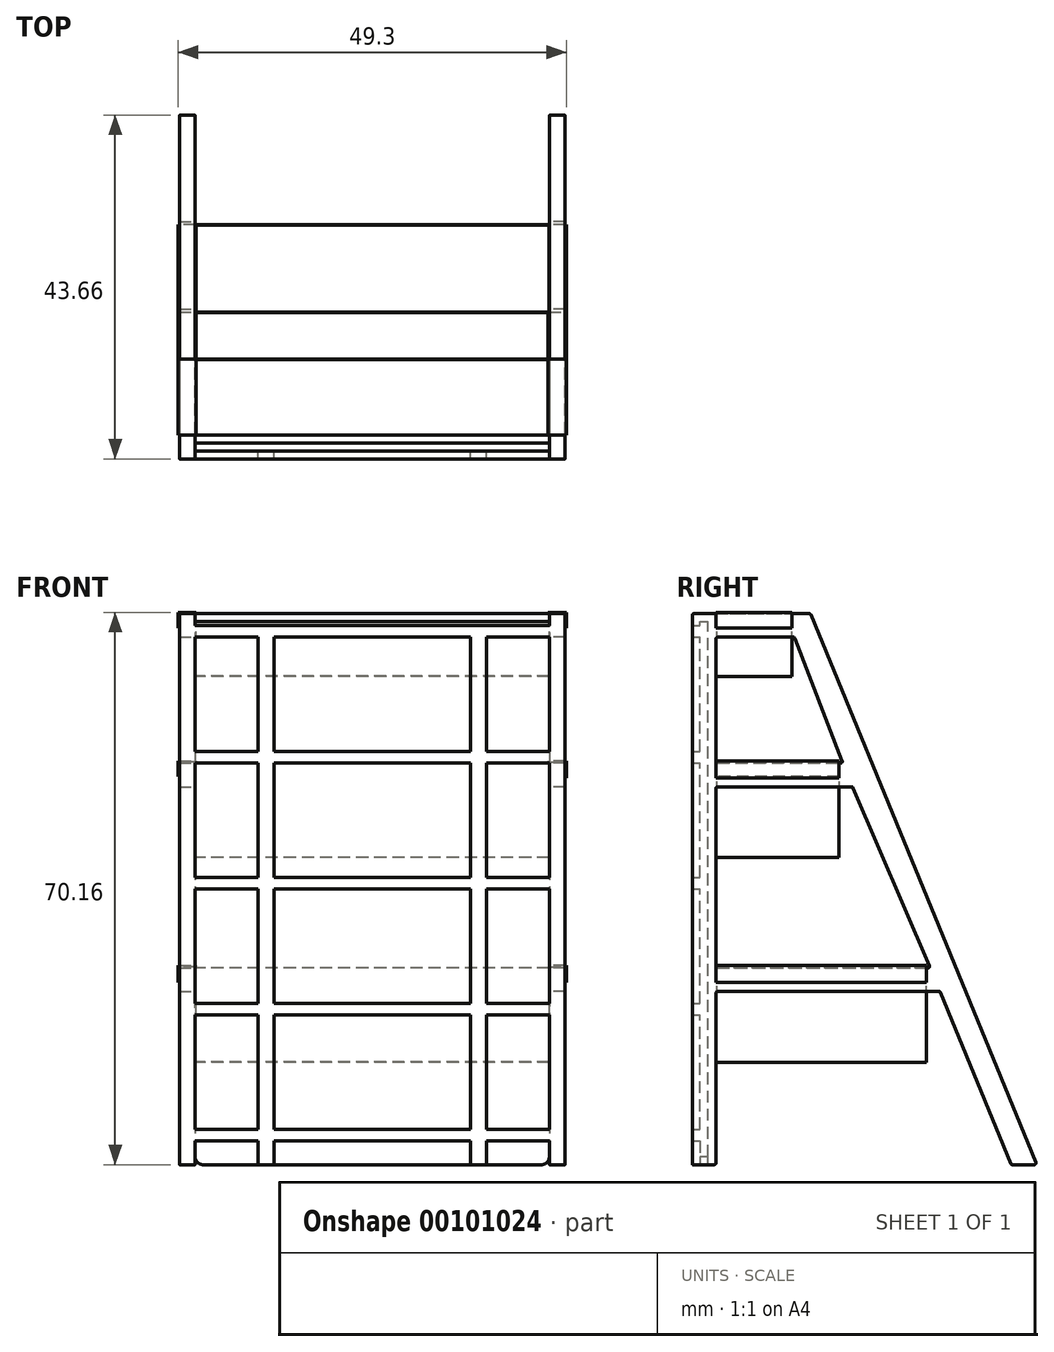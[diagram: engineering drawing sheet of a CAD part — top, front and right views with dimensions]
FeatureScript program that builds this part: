
annotation { "Feature Type Name" : "Feature", "Feature Type Description" : "" }
export const myFeature = defineFeature(function(context is Context, id is Id, definition is map)
    precondition{}
    {
        {
            var Q0;
            Q0=qCreatedBy(makeId("Right.planeOp"),FACE);
            var sketch = newSketch(context, id + "F0", { "sketchPlane" : qUnion([Q0])});
            skLineSegment(sketch, "E0", {"start": v(0, 0.2) * mm, "end": v(0, 69.8) * mm});
            skLineSegment(sketch, "E1", {"start": v(0.2, 70) * mm, "end": v(14.87, 70) * mm});
            skLineSegment(sketch, "E2", {"start": v(15.05, 69.88) * mm, "end": v(43.64, 0.28) * mm});
            skLineSegment(sketch, "E3", {"start": v(43.46, 0) * mm, "end": v(40.65, 0) * mm});
            skLineSegment(sketch, "E4", {"start": v(12.86, 67) * mm, "end": v(3.2, 67) * mm});
            skLineSegment(sketch, "E5", {"start": v(2.8, 0) * mm, "end": v(0.2, 0) * mm});
            skLineSegment(sketch, "E6", {"start": v(3.2, 51) * mm, "end": v(18.85, 51) * mm});
            skLineSegment(sketch, "E7", {"start": v(13.04, 66.87) * mm, "end": v(19.04, 51.27) * mm});
            skLineSegment(sketch, "E8", {"start": v(3, 66.8) * mm, "end": v(3, 51.2) * mm});
            skLineSegment(sketch, "E9", {"start": v(3.2, 48) * mm, "end": v(20.25, 48) * mm});
            skLineSegment(sketch, "E10", {"start": v(3, 47.8) * mm, "end": v(3, 25.2) * mm});
            skLineSegment(sketch, "E11", {"start": v(3.2, 25) * mm, "end": v(29.94, 25) * mm});
            skLineSegment(sketch, "E12", {"start": v(3.2, 22) * mm, "end": v(31.34, 22) * mm});
            skLineSegment(sketch, "E13", {"start": v(70.75, 0) * mm, "end": v(70.75, 13) * mm});
            skLineSegment(sketch, "E14", {"start": v(70.75, 13) * mm, "end": v(70.75, 25) * mm});
            skLineSegment(sketch, "E15", {"start": v(70.75, 25) * mm, "end": v(70.75, 40) * mm});
            skLineSegment(sketch, "E16", {"start": v(70.75, 40) * mm, "end": v(70.75, 52) * mm});
            skLineSegment(sketch, "E17", {"start": v(70.75, 52) * mm, "end": v(70.75, 62) * mm});
            skLineSegment(sketch, "E18", {"start": v(70.75, 62) * mm, "end": v(70.75, 70) * mm});
            skLineSegment(sketch, "E19", {"start": v(3, 0.2) * mm, "end": v(3, 21.8) * mm});
            skLineSegment(sketch, "E20", {"start": v(20.43, 47.88) * mm, "end": v(30.13, 25.28) * mm});
            skLineSegment(sketch, "E21", {"start": v(31.53, 21.88) * mm, "end": v(40.46, 0.12) * mm});
            skPoint(sketch, "E22.visualSharp", {"position": v(3, 25) * mm});
            skArc(sketch, "E22.filletArc", {"start": v(3, 25.2) * mm, "mid": v(3.06, 25.06) * mm, "end": v(3.2, 25) * mm});
            skPoint(sketch, "E23.visualSharp", {"position": v(3, 22) * mm});
            skArc(sketch, "E23.filletArc", {"start": v(3.2, 22) * mm, "mid": v(3.06, 21.94) * mm, "end": v(3, 21.8) * mm});
            skPoint(sketch, "E24.visualSharp", {"position": v(31.48, 22) * mm});
            skArc(sketch, "E24.filletArc", {"start": v(31.53, 21.88) * mm, "mid": v(31.45, 21.97) * mm, "end": v(31.34, 22) * mm});
            skPoint(sketch, "E25.visualSharp", {"position": v(3, 0) * mm});
            skArc(sketch, "E25.filletArc", {"start": v(2.8, 0) * mm, "mid": v(2.94, 0.06) * mm, "end": v(3, 0.2) * mm});
            skPoint(sketch, "E26.visualSharp", {"position": v(40.51, 0) * mm});
            skArc(sketch, "E26.filletArc", {"start": v(40.46, 0.12) * mm, "mid": v(40.54, 0.03) * mm, "end": v(40.65, 0) * mm});
            skPoint(sketch, "E27.visualSharp", {"position": v(15, 70) * mm});
            skArc(sketch, "E27.filletArc", {"start": v(15.05, 69.88) * mm, "mid": v(14.98, 69.97) * mm, "end": v(14.87, 70) * mm});
            skPoint(sketch, "E28.visualSharp", {"position": v(0, 70) * mm});
            skArc(sketch, "E28.filletArc", {"start": v(0.2, 70) * mm, "mid": v(0.06, 69.94) * mm, "end": v(0, 69.8) * mm});
            skPoint(sketch, "E29.visualSharp", {"position": v(3, 67) * mm});
            skArc(sketch, "E29.filletArc", {"start": v(3.2, 67) * mm, "mid": v(3.06, 66.94) * mm, "end": v(3, 66.8) * mm});
            skPoint(sketch, "E30.visualSharp", {"position": v(19.14, 51) * mm});
            skArc(sketch, "E30.filletArc", {"start": v(18.85, 51) * mm, "mid": v(19.02, 51.09) * mm, "end": v(19.04, 51.27) * mm});
            skPoint(sketch, "E31.visualSharp", {"position": v(3, 51) * mm});
            skArc(sketch, "E31.filletArc", {"start": v(3, 51.2) * mm, "mid": v(3.06, 51.06) * mm, "end": v(3.2, 51) * mm});
            skPoint(sketch, "E32.visualSharp", {"position": v(20.38, 48) * mm});
            skArc(sketch, "E32.filletArc", {"start": v(20.43, 47.88) * mm, "mid": v(20.36, 47.97) * mm, "end": v(20.25, 48) * mm});
            skPoint(sketch, "E33.visualSharp", {"position": v(3, 48) * mm});
            skArc(sketch, "E33.filletArc", {"start": v(3.2, 48) * mm, "mid": v(3.06, 47.94) * mm, "end": v(3, 47.8) * mm});
            skPoint(sketch, "E34.visualSharp", {"position": v(30.25, 25) * mm});
            skArc(sketch, "E34.filletArc", {"start": v(29.94, 25) * mm, "mid": v(30.11, 25.09) * mm, "end": v(30.13, 25.28) * mm});
            skPoint(sketch, "E35.visualSharp", {"position": v(43.76, 0) * mm});
            skArc(sketch, "E35.filletArc", {"start": v(43.46, 0) * mm, "mid": v(43.62, 0.09) * mm, "end": v(43.64, 0.28) * mm});
            skPoint(sketch, "E36.visualSharp", {"position": v(0, 0) * mm});
            skArc(sketch, "E36.filletArc", {"start": v(0, 0.2) * mm, "mid": v(0.06, 0.06) * mm, "end": v(0.2, 0) * mm});
            skPoint(sketch, "E37.visualSharp", {"position": v(13, 67) * mm});
            skArc(sketch, "E37.filletArc", {"start": v(13.04, 66.87) * mm, "mid": v(12.97, 66.96) * mm, "end": v(12.86, 67) * mm});
            skLineSegment(sketch, "E38", {"start": v(4.02, 67) * mm, "end": v(4.02, 70) * mm});
            skLineSegment(sketch, "E39.bottom", {"start": v(1, 3) * mm, "end": v(2, 3) * mm});
            skLineSegment(sketch, "E39.top", {"start": v(1, 9) * mm, "end": v(2, 9) * mm});
            skLineSegment(sketch, "E39.left", {"start": v(1, 3) * mm, "end": v(1, 9) * mm});
            skLineSegment(sketch, "E39.right", {"start": v(2, 3) * mm, "end": v(2, 9) * mm});
            skLineSegment(sketch, "E40.0.1.0", {"start": v(1, 39) * mm, "end": v(2, 39) * mm});
            skLineSegment(sketch, "E40.0.1.1", {"start": v(1, 33) * mm, "end": v(1, 39) * mm});
            skLineSegment(sketch, "E40.0.1.2", {"start": v(2, 33) * mm, "end": v(2, 39) * mm});
            skLineSegment(sketch, "E40.0.1.3", {"start": v(1, 33) * mm, "end": v(2, 33) * mm});
            skLineSegment(sketch, "E40.0.2.0", {"start": v(1, 69) * mm, "end": v(2, 69) * mm});
            skLineSegment(sketch, "E40.0.2.1", {"start": v(1, 63) * mm, "end": v(1, 69) * mm});
            skLineSegment(sketch, "E40.0.2.2", {"start": v(2, 63) * mm, "end": v(2, 69) * mm});
            skLineSegment(sketch, "E40.0.2.3", {"start": v(1, 63) * mm, "end": v(2, 63) * mm});
            skLineSegment(sketch, "E40.direction1", {"start": v(1, 9) * mm, "end": v(26, 9) * mm, "construction": true});
            skLineSegment(sketch, "E40.direction2", {"start": v(1, 9) * mm, "end": v(1, 39) * mm, "construction": true});
            skLineSegment(sketch, "E41", {"start": v(1, 3) * mm, "end": v(1, 0) * mm});
            skSolve(sketch);
        }
        {
            var Q0;
            Q0=qCreatedBy(makeId("Front.planeOp"),FACE);
            var sketch = newSketch(context, id + "F1", { "sketchPlane" : qUnion([Q0])});
            skLineSegment(sketch, "E42", {"start": v(0, 0) * mm, "end": v(0, 13) * mm});
            skLineSegment(sketch, "E43.bottom", {"start": v(0, 13) * mm, "end": v(-45, 13) * mm});
            skLineSegment(sketch, "E43.top", {"start": v(0, 25) * mm, "end": v(-45, 25) * mm});
            skLineSegment(sketch, "E43.left", {"start": v(0, 13) * mm, "end": v(0, 25) * mm});
            skLineSegment(sketch, "E43.right", {"start": v(-45, 13) * mm, "end": v(-45, 25) * mm});
            skLineSegment(sketch, "E44", {"start": v(0, 25) * mm, "end": v(0, 39) * mm});
            skLineSegment(sketch, "E45.bottom", {"start": v(0, 39) * mm, "end": v(-45, 39) * mm});
            skLineSegment(sketch, "E45.top", {"start": v(0, 51) * mm, "end": v(-45, 51) * mm});
            skLineSegment(sketch, "E45.left", {"start": v(0, 39) * mm, "end": v(0, 51) * mm});
            skLineSegment(sketch, "E45.right", {"start": v(-45, 39) * mm, "end": v(-45, 51) * mm});
            skLineSegment(sketch, "E46.bottom", {"start": v(0, 62) * mm, "end": v(-45, 62) * mm});
            skLineSegment(sketch, "E46.top", {"start": v(0, 70) * mm, "end": v(-45, 70) * mm});
            skLineSegment(sketch, "E46.left", {"start": v(0, 62) * mm, "end": v(0, 70) * mm});
            skLineSegment(sketch, "E46.right", {"start": v(-45, 62) * mm, "end": v(-45, 70) * mm});
            skLineSegment(sketch, "E47", {"start": v(0, 70) * mm, "end": v(0, 70.01) * mm});
            skLineSegment(sketch, "E48", {"start": v(0, 70.01) * mm, "end": v(2, 70.01) * mm});
            skLineSegment(sketch, "E49", {"start": v(2, 70.01) * mm, "end": v(2, 68.16) * mm});
            skLineSegment(sketch, "E50", {"start": v(2, 68.16) * mm, "end": v(2.15, 68.16) * mm});
            skLineSegment(sketch, "E51", {"start": v(2.15, 68.16) * mm, "end": v(2.15, 70.16) * mm});
            skLineSegment(sketch, "E52", {"start": v(2.15, 70.16) * mm, "end": v(-0.15, 70.16) * mm});
            skLineSegment(sketch, "E53", {"start": v(-0.15, 70.16) * mm, "end": v(-0.15, 68.16) * mm});
            skLineSegment(sketch, "E54", {"start": v(0, 69.73) * mm, "end": v(0, 70) * mm});
            skLineSegment(sketch, "E55", {"start": v(-45, 70) * mm, "end": v(-45, 70.01) * mm});
            skLineSegment(sketch, "E56", {"start": v(-45, 70.01) * mm, "end": v(-47, 70.01) * mm});
            skLineSegment(sketch, "E57", {"start": v(-47, 70.01) * mm, "end": v(-47, 68.16) * mm});
            skLineSegment(sketch, "E58", {"start": v(-47, 68.16) * mm, "end": v(-47.15, 68.16) * mm});
            skLineSegment(sketch, "E59", {"start": v(-47.15, 68.16) * mm, "end": v(-47.15, 70.16) * mm});
            skLineSegment(sketch, "E60", {"start": v(-47.15, 70.16) * mm, "end": v(-44.85, 70.16) * mm});
            skLineSegment(sketch, "E61", {"start": v(-44.85, 70.16) * mm, "end": v(-44.85, 68.16) * mm});
            skLineSegment(sketch, "E62", {"start": v(-44.85, 68.16) * mm, "end": v(-45, 68.16) * mm});
            skLineSegment(sketch, "E63", {"start": v(-45, 51) * mm, "end": v(-45, 51.15) * mm});
            skLineSegment(sketch, "E64", {"start": v(-45, 51.15) * mm, "end": v(-47, 51.15) * mm});
            skLineSegment(sketch, "E65", {"start": v(-47, 51.15) * mm, "end": v(-47, 49.3) * mm});
            skLineSegment(sketch, "E66", {"start": v(-47, 49.3) * mm, "end": v(-47.15, 49.3) * mm});
            skLineSegment(sketch, "E67", {"start": v(-47.15, 49.3) * mm, "end": v(-47.15, 51.3) * mm});
            skLineSegment(sketch, "E68", {"start": v(-47.15, 51.3) * mm, "end": v(-44.85, 51.3) * mm});
            skLineSegment(sketch, "E69", {"start": v(-44.85, 51.3) * mm, "end": v(-44.85, 51) * mm});
            skLineSegment(sketch, "E70", {"start": v(0, 51) * mm, "end": v(0, 51.15) * mm});
            skLineSegment(sketch, "E71", {"start": v(0, 51.15) * mm, "end": v(2, 51.15) * mm});
            skLineSegment(sketch, "E72", {"start": v(2, 51.15) * mm, "end": v(2, 49.15) * mm});
            skLineSegment(sketch, "E73", {"start": v(2, 49.15) * mm, "end": v(2.15, 49.15) * mm});
            skLineSegment(sketch, "E74", {"start": v(2.15, 49.15) * mm, "end": v(2.15, 51.3) * mm});
            skLineSegment(sketch, "E75", {"start": v(2.15, 51.3) * mm, "end": v(-0.15, 51.3) * mm});
            skLineSegment(sketch, "E76", {"start": v(-0.15, 51.3) * mm, "end": v(-0.15, 51) * mm});
            skLineSegment(sketch, "E77", {"start": v(0, 25) * mm, "end": v(0, 25.15) * mm});
            skLineSegment(sketch, "E78", {"start": v(0, 25.15) * mm, "end": v(2, 25.15) * mm});
            skLineSegment(sketch, "E79", {"start": v(2, 25.15) * mm, "end": v(2, 23.15) * mm});
            skLineSegment(sketch, "E80", {"start": v(2, 23.15) * mm, "end": v(2.15, 23.15) * mm});
            skLineSegment(sketch, "E81", {"start": v(2.15, 23.15) * mm, "end": v(2.15, 25.3) * mm});
            skLineSegment(sketch, "E82", {"start": v(2.15, 25.3) * mm, "end": v(-0.15, 25.3) * mm});
            skLineSegment(sketch, "E83", {"start": v(-0.15, 25.3) * mm, "end": v(-0.15, 25) * mm});
            skLineSegment(sketch, "E84", {"start": v(-45, 25) * mm, "end": v(-45, 25.15) * mm});
            skLineSegment(sketch, "E85", {"start": v(-45, 25.15) * mm, "end": v(-47, 25.15) * mm});
            skLineSegment(sketch, "E86", {"start": v(-47, 25.15) * mm, "end": v(-47, 23.15) * mm});
            skLineSegment(sketch, "E87", {"start": v(-47, 23.15) * mm, "end": v(-47.15, 23.15) * mm});
            skLineSegment(sketch, "E88", {"start": v(-47.15, 23.15) * mm, "end": v(-47.15, 25.3) * mm});
            skLineSegment(sketch, "E89", {"start": v(-47.15, 25.3) * mm, "end": v(-44.85, 25.3) * mm});
            skLineSegment(sketch, "E90", {"start": v(-44.85, 25.3) * mm, "end": v(-44.85, 25) * mm});
            skSolve(sketch);
        }
        {
            var Q0;
            Q0=makeQuery(id+"F0.imprint","IMPRINT",FACE,{"disambiguationData":[TD([[makeQuery(id+"F0.imprint","IMPRINT",EDGE,{"derivedFrom":sQuery(id+"F0.wireOp",EDGE,"E0")}),-1.0]])]});
            extrude(context, id + "F2", {"entities" : qUnion([Q0]), "depth" : 2 * mm});
        }
        {
            var Q0;
            Q0=qSketchRegion(id+"F0",true);
            extrude(context, id + "F3", {"entities" : qUnion([Q0]), "oppositeDirection" : true, "depth" : 47 * mm, "hasSecondDirection" : true, "secondDirectionOppositeDirection" : true, "secondDirectionDepth" : 45 * mm});
        }
        {
            var Q0;
            Q0=makeQuery(id+"F1.imprint","IMPRINT",FACE,{"disambiguationData":[TD([[makeQuery(id+"F1.imprint","IMPRINT",EDGE,{"derivedFrom":sQuery(id+"F1.wireOp",EDGE,"E46.bottom")}),-1.0]])]});
            var Q1;
            {var subQ0=sQuery(id+"F1.wireOp",EDGE,"E47");Q1=makeQuery(id+"F1.imprint","IMPRINT",FACE,{"disambiguationData":[TD([[makeQuery(id+"F1.imprint","IMPRINT",EDGE,{"derivedFrom":subQ0}),1.0]])]});}
            var Q2;
            {var subQ5=sQuery(id+"F1.wireOp",EDGE,"E62");Q2=makeQuery(id+"F1.imprint","IMPRINT",FACE,{"disambiguationData":[TD([[makeQuery(id+"F1.imprint","IMPRINT",EDGE,{"derivedFrom":subQ5}),-1.0]])]});}
            var Q3;
            {var subQ0=sQuery(id+"F1.wireOp",EDGE,"E55");Q3=makeQuery(id+"F1.imprint","IMPRINT",FACE,{"disambiguationData":[TD([[makeQuery(id+"F1.imprint","IMPRINT",EDGE,{"derivedFrom":subQ0}),-1.0]])]});}
            extrude(context, id + "F4", {"entities" : qUnion([Q0, Q1, Q2, Q3]), "oppositeDirection" : true, "depth" : 12.65 * mm, "hasSecondDirection" : true, "secondDirectionOppositeDirection" : true, "secondDirectionDepth" : 3 * mm});
        }
        {
            var Q0;
            Q0=makeQuery(id+"F1.imprint","IMPRINT",FACE,{"disambiguationData":[TD([[makeQuery(id+"F1.imprint","IMPRINT",EDGE,{"derivedFrom":sQuery(id+"F1.wireOp",EDGE,"E45.bottom")}),-1.0]])]});
            var Q1;
            {var subQ0=sQuery(id+"F1.wireOp",EDGE,"E70");Q1=makeQuery(id+"F1.imprint","IMPRINT",FACE,{"disambiguationData":[TD([[makeQuery(id+"F1.imprint","IMPRINT",EDGE,{"derivedFrom":subQ0}),1.0]])]});}
            var Q2;
            {var subQ0=sQuery(id+"F1.wireOp",EDGE,"E63");Q2=makeQuery(id+"F1.imprint","IMPRINT",FACE,{"disambiguationData":[TD([[makeQuery(id+"F1.imprint","IMPRINT",EDGE,{"derivedFrom":subQ0}),-1.0]])]});}
            extrude(context, id + "F5", {"entities" : qUnion([Q0, Q1, Q2]), "oppositeDirection" : true, "depth" : 18.65 * mm, "hasSecondDirection" : true, "secondDirectionOppositeDirection" : true, "secondDirectionDepth" : 3 * mm});
        }
        {
            var Q0;
            Q0=makeQuery(id+"F1.imprint","IMPRINT",FACE,{"disambiguationData":[TD([[makeQuery(id+"F1.imprint","IMPRINT",EDGE,{"derivedFrom":sQuery(id+"F1.wireOp",EDGE,"E43.bottom")}),-1.0]])]});
            var Q1;
            {var subQ0=sQuery(id+"F1.wireOp",EDGE,"E84");Q1=makeQuery(id+"F1.imprint","IMPRINT",FACE,{"disambiguationData":[TD([[makeQuery(id+"F1.imprint","IMPRINT",EDGE,{"derivedFrom":subQ0}),-1.0]])]});}
            var Q2;
            {var subQ0=sQuery(id+"F1.wireOp",EDGE,"E78");Q2=makeQuery(id+"F1.imprint","IMPRINT",FACE,{"disambiguationData":[TD([[makeQuery(id+"F1.imprint","IMPRINT",EDGE,{"derivedFrom":subQ0}),1.0]])]});}
            var Q3;
            {var subQ0=sQuery(id+"F1.wireOp",EDGE,"E77");Q3=makeQuery(id+"F1.imprint","IMPRINT",FACE,{"disambiguationData":[TD([[makeQuery(id+"F1.imprint","IMPRINT",EDGE,{"derivedFrom":subQ0}),1.0]])]});}
            extrude(context, id + "F6", {"entities" : qUnion([Q0, Q1, Q2, Q3]), "oppositeDirection" : true, "depth" : 29.74 * mm, "hasSecondDirection" : true, "secondDirectionOppositeDirection" : true, "secondDirectionDepth" : 3 * mm});
        }
        {
            var Q0;
            Q0=qCreatedBy(makeId("Front.planeOp"),FACE);
            var sketch = newSketch(context, id + "F7", { "sketchPlane" : qUnion([Q0])});
            skLineSegment(sketch, "E91.bottom", {"start": v(-1, 0) * mm, "end": v(-44, 0) * mm});
            skLineSegment(sketch, "E92", {"start": v(0, 3) * mm, "end": v(2, 3) * mm});
            skLineSegment(sketch, "E93", {"start": v(2, 3) * mm, "end": v(2, 9) * mm});
            skLineSegment(sketch, "E94", {"start": v(2, 9) * mm, "end": v(0, 9) * mm});
            skLineSegment(sketch, "E95", {"start": v(0, 3) * mm, "end": v(0, 1) * mm});
            skLineSegment(sketch, "E96.0.1.0", {"start": v(2, 39) * mm, "end": v(0, 39) * mm});
            skLineSegment(sketch, "E96.0.1.1", {"start": v(2, 33) * mm, "end": v(2, 39) * mm});
            skLineSegment(sketch, "E96.0.1.2", {"start": v(0, 33) * mm, "end": v(2, 33) * mm});
            skLineSegment(sketch, "E96.0.2.0", {"start": v(2, 69) * mm, "end": v(0, 69) * mm});
            skLineSegment(sketch, "E96.0.2.1", {"start": v(2, 63) * mm, "end": v(2, 69) * mm});
            skLineSegment(sketch, "E96.0.2.2", {"start": v(0, 63) * mm, "end": v(2, 63) * mm});
            skLineSegment(sketch, "E96.direction1", {"start": v(0, 9) * mm, "end": v(25, 9) * mm, "construction": true});
            skLineSegment(sketch, "E96.direction2", {"start": v(0, 9) * mm, "end": v(0, 39) * mm, "construction": true});
            skLineSegment(sketch, "E97", {"start": v(0, 9) * mm, "end": v(0, 33) * mm});
            skLineSegment(sketch, "E98", {"start": v(0, 39) * mm, "end": v(0, 63) * mm});
            skLineSegment(sketch, "E99", {"start": v(-45, 3) * mm, "end": v(-47, 3) * mm});
            skLineSegment(sketch, "E100", {"start": v(-47, 3) * mm, "end": v(-47, 9) * mm});
            skLineSegment(sketch, "E101", {"start": v(-47, 9) * mm, "end": v(-45, 9) * mm});
            skLineSegment(sketch, "E102.0.1.0", {"start": v(-47, 39) * mm, "end": v(-45, 39) * mm});
            skLineSegment(sketch, "E102.0.1.1", {"start": v(-47, 33) * mm, "end": v(-47, 39) * mm});
            skLineSegment(sketch, "E102.0.1.2", {"start": v(-45, 33) * mm, "end": v(-47, 33) * mm});
            skLineSegment(sketch, "E102.0.2.0", {"start": v(-47, 69) * mm, "end": v(-45, 69) * mm});
            skLineSegment(sketch, "E102.0.2.1", {"start": v(-47, 63) * mm, "end": v(-47, 69) * mm});
            skLineSegment(sketch, "E102.0.2.2", {"start": v(-45, 63) * mm, "end": v(-47, 63) * mm});
            skLineSegment(sketch, "E102.direction1", {"start": v(-47, 9) * mm, "end": v(-22, 9) * mm, "construction": true});
            skLineSegment(sketch, "E102.direction2", {"start": v(-47, 9) * mm, "end": v(-47, 39) * mm, "construction": true});
            skLineSegment(sketch, "E103", {"start": v(-45, 3) * mm, "end": v(-45, 1) * mm});
            skLineSegment(sketch, "E104", {"start": v(-45, 9) * mm, "end": v(-45, 33) * mm});
            skLineSegment(sketch, "E105", {"start": v(-45, 39) * mm, "end": v(-45, 63) * mm});
            skPoint(sketch, "E106.visualSharp", {"position": v(0, 70) * mm});
            skPoint(sketch, "E107.visualSharp", {"position": v(-45, 0) * mm});
            skArc(sketch, "E107.filletArc", {"start": v(-45, 1) * mm, "mid": v(-44.7, 0.3) * mm, "end": v(-44, 0) * mm});
            skPoint(sketch, "E108.visualSharp", {"position": v(0, 0) * mm});
            skArc(sketch, "E108.filletArc", {"start": v(-1, 0) * mm, "mid": v(-0.3, 0.3) * mm, "end": v(0, 1) * mm});
            skLineSegment(sketch, "E109", {"start": v(-45, 69) * mm, "end": v(0, 69) * mm});
            skSolve(sketch);
        }
        {
            var Q0;
            Q0 = qSketchRegion(id + "F7", true);
            extrude(context, id + "F8", {"entities" : qUnion([Q0]), "oppositeDirection" : true, "depth" : 2 * mm, "hasSecondDirection" : true, "secondDirectionOppositeDirection" : true, "secondDirectionDepth" : 1 * mm});
        }
        {
            var Q0;
            Q0=makeQuery(id+"F8.opExtrude","CAP_FACE",FACE,{"disambiguationData":[OSD([sQuery(id+"F7.wireOp",EDGE,"E91.bottom"),sQuery(id+"F7.wireOp",EDGE,"E92"),sQuery(id+"F7.wireOp",EDGE,"E93"),sQuery(id+"F7.wireOp",EDGE,"E94"),sQuery(id+"F7.wireOp",EDGE,"E95"),sQuery(id+"F7.wireOp",EDGE,"E96.0.1.0"),sQuery(id+"F7.wireOp",EDGE,"E96.0.1.1"),sQuery(id+"F7.wireOp",EDGE,"E96.0.1.2"),sQuery(id+"F7.wireOp",EDGE,"E96.0.2.0"),sQuery(id+"F7.wireOp",EDGE,"E96.0.2.1"),sQuery(id+"F7.wireOp",EDGE,"E96.0.2.2"),sQuery(id+"F7.wireOp",EDGE,"E97"),sQuery(id+"F7.wireOp",EDGE,"E98"),sQuery(id+"F7.wireOp",EDGE,"E99"),sQuery(id+"F7.wireOp",EDGE,"E100"),sQuery(id+"F7.wireOp",EDGE,"E101"),sQuery(id+"F7.wireOp",EDGE,"E102.0.1.0"),sQuery(id+"F7.wireOp",EDGE,"E102.0.1.1"),sQuery(id+"F7.wireOp",EDGE,"E102.0.1.2"),sQuery(id+"F7.wireOp",EDGE,"E102.0.2.0"),sQuery(id+"F7.wireOp",EDGE,"E102.0.2.1"),sQuery(id+"F7.wireOp",EDGE,"E102.0.2.2"),sQuery(id+"F7.wireOp",EDGE,"E103"),sQuery(id+"F7.wireOp",EDGE,"E104"),sQuery(id+"F7.wireOp",EDGE,"E105"),sQuery(id+"F7.wireOp",EDGE,"E107.filletArc"),sQuery(id+"F7.wireOp",EDGE,"E108.filletArc"),sQuery(id+"F7.wireOp",EDGE,"E109")])],"isStart":true});
            var sketch = newSketch(context, id + "F9", { "sketchPlane" : qUnion([Q0])});
            skLineSegment(sketch, "E110", {"start": v(-45, 3) * mm, "end": v(-45, 4.5) * mm});
            skLineSegment(sketch, "E111", {"start": v(0, 4.5) * mm, "end": v(0, 3) * mm});
            skLineSegment(sketch, "E112.0.1.0", {"start": v(-45, 19) * mm, "end": v(-45, 20.5) * mm});
            skLineSegment(sketch, "E112.0.1.3", {"start": v(0, 20.5) * mm, "end": v(0, 19) * mm});
            skLineSegment(sketch, "E112.0.2.0", {"start": v(-45, 35) * mm, "end": v(-45, 36.5) * mm});
            skLineSegment(sketch, "E112.0.2.3", {"start": v(0, 36.5) * mm, "end": v(0, 35) * mm});
            skLineSegment(sketch, "E112.0.3.0", {"start": v(-45, 51) * mm, "end": v(-45, 52.5) * mm});
            skLineSegment(sketch, "E112.0.3.3", {"start": v(0, 52.5) * mm, "end": v(0, 51) * mm});
            skLineSegment(sketch, "E112.0.4.0", {"start": v(-45, 67) * mm, "end": v(-45, 68.5) * mm});
            skLineSegment(sketch, "E112.0.4.1", {"start": v(-45, 68.5) * mm, "end": v(0, 68.5) * mm});
            skLineSegment(sketch, "E112.0.4.3", {"start": v(0, 68.5) * mm, "end": v(0, 67) * mm});
            skLineSegment(sketch, "E112.direction2", {"start": v(-45, 3) * mm, "end": v(-45, 19) * mm, "construction": true});
            skLineSegment(sketch, "E113", {"start": v(-45, 67) * mm, "end": v(-37, 67) * mm});
            skLineSegment(sketch, "E114", {"start": v(-37, 0) * mm, "end": v(-35, 0) * mm});
            skLineSegment(sketch, "E115.1.0.2", {"start": v(-10, 0) * mm, "end": v(-8, 0) * mm});
            skLineSegment(sketch, "E115.direction1", {"start": v(-37, 0) * mm, "end": v(-10, 0) * mm, "construction": true});
            skLineSegment(sketch, "E116", {"start": v(-35, 67) * mm, "end": v(-10, 67) * mm});
            skLineSegment(sketch, "E117", {"start": v(-8, 67) * mm, "end": v(0, 67) * mm});
            skLineSegment(sketch, "E118", {"start": v(0, 52.5) * mm, "end": v(-8, 52.5) * mm});
            skLineSegment(sketch, "E119", {"start": v(-45, 52.5) * mm, "end": v(-37, 52.5) * mm});
            skLineSegment(sketch, "E120", {"start": v(-37, 52.5) * mm, "end": v(-37, 67) * mm});
            skLineSegment(sketch, "E121", {"start": v(-8, 52.5) * mm, "end": v(-8, 67) * mm});
            skLineSegment(sketch, "E122", {"start": v(-35, 52.5) * mm, "end": v(-10, 52.5) * mm});
            skLineSegment(sketch, "E123", {"start": v(-35, 67) * mm, "end": v(-35, 52.5) * mm});
            skLineSegment(sketch, "E124", {"start": v(-37, 51) * mm, "end": v(-37, 36.5) * mm});
            skLineSegment(sketch, "E125", {"start": v(-37, 36.5) * mm, "end": v(-45, 36.5) * mm});
            skLineSegment(sketch, "E126", {"start": v(-37, 35) * mm, "end": v(-37, 20.5) * mm});
            skLineSegment(sketch, "E127", {"start": v(-37, 20.5) * mm, "end": v(-45, 20.5) * mm});
            skLineSegment(sketch, "E128", {"start": v(-37, 19) * mm, "end": v(-37, 4.5) * mm});
            skLineSegment(sketch, "E129", {"start": v(-37, 4.5) * mm, "end": v(-45, 4.5) * mm});
            skLineSegment(sketch, "E130", {"start": v(-37, 0) * mm, "end": v(-37, 3) * mm});
            skLineSegment(sketch, "E131", {"start": v(-37, 3) * mm, "end": v(-45, 3) * mm});
            skLineSegment(sketch, "E132", {"start": v(-35, 51) * mm, "end": v(-35, 36.5) * mm});
            skLineSegment(sketch, "E133", {"start": v(-35, 36.5) * mm, "end": v(-10, 36.5) * mm});
            skLineSegment(sketch, "E134", {"start": v(-10, 36.5) * mm, "end": v(-10, 51) * mm});
            skLineSegment(sketch, "E135", {"start": v(-10, 51) * mm, "end": v(-35, 51) * mm});
            skLineSegment(sketch, "E136", {"start": v(-8, 51) * mm, "end": v(0, 51) * mm});
            skLineSegment(sketch, "E137", {"start": v(-8, 51) * mm, "end": v(-8, 36.5) * mm});
            skLineSegment(sketch, "E138", {"start": v(-8, 36.5) * mm, "end": v(0, 36.5) * mm});
            skLineSegment(sketch, "E139", {"start": v(0, 35) * mm, "end": v(-8, 35) * mm});
            skLineSegment(sketch, "E140", {"start": v(-8, 35) * mm, "end": v(-8, 20.5) * mm});
            skLineSegment(sketch, "E141", {"start": v(-8, 20.5) * mm, "end": v(0, 20.5) * mm});
            skLineSegment(sketch, "E142", {"start": v(0, 19) * mm, "end": v(-8, 19) * mm});
            skLineSegment(sketch, "E143", {"start": v(-8, 19) * mm, "end": v(-8, 4.5) * mm});
            skLineSegment(sketch, "E144", {"start": v(-8, 4.5) * mm, "end": v(0, 4.5) * mm});
            skLineSegment(sketch, "E145", {"start": v(0, 3) * mm, "end": v(-8, 3) * mm});
            skLineSegment(sketch, "E146", {"start": v(-8, 3) * mm, "end": v(-8, 0) * mm});
            skLineSegment(sketch, "E147", {"start": v(-37, 51) * mm, "end": v(-45, 51) * mm});
            skLineSegment(sketch, "E148", {"start": v(-37, 35) * mm, "end": v(-45, 35) * mm});
            skLineSegment(sketch, "E149", {"start": v(-35, 35) * mm, "end": v(-10, 35) * mm});
            skLineSegment(sketch, "E150", {"start": v(-10, 35) * mm, "end": v(-10, 20.5) * mm});
            skLineSegment(sketch, "E151", {"start": v(-10, 20.5) * mm, "end": v(-35, 20.5) * mm});
            skLineSegment(sketch, "E152", {"start": v(-35, 20.5) * mm, "end": v(-35, 35) * mm});
            skLineSegment(sketch, "E153", {"start": v(-35, 19) * mm, "end": v(-10, 19) * mm});
            skLineSegment(sketch, "E154", {"start": v(-10, 19) * mm, "end": v(-10, 4.5) * mm});
            skLineSegment(sketch, "E155", {"start": v(-10, 4.5) * mm, "end": v(-35, 4.5) * mm});
            skLineSegment(sketch, "E156", {"start": v(-35, 4.5) * mm, "end": v(-35, 19) * mm});
            skLineSegment(sketch, "E157", {"start": v(-35, 3) * mm, "end": v(-35, 0) * mm});
            skLineSegment(sketch, "E158", {"start": v(-10, 0) * mm, "end": v(-10, 3) * mm});
            skLineSegment(sketch, "E159", {"start": v(-10, 3) * mm, "end": v(-35, 3) * mm});
            skLineSegment(sketch, "E160", {"start": v(-37, 19) * mm, "end": v(-45, 19) * mm});
            skLineSegment(sketch, "E161", {"start": v(-10, 67) * mm, "end": v(-10, 52.5) * mm});
            skSolve(sketch);
        }
        {
            var Q0;
            Q0 = qSketchRegion(id + "F9", true);
            extrude(context, id + "F10", {"entities" : qUnion([Q0]), "operationType" : NewBodyOperationType.ADD, "depth" : 1 * mm, "hasSecondDirection" : true, "secondDirectionOppositeDirection" : true, "secondDirectionDepth" : 1 * mm});
        }
        {
            var Q0;
            Q0=qCreatedBy(makeId("Top.planeOp"),FACE);
            var sketch = newSketch(context, id + "F11", { "sketchPlane" : qUnion([Q0])});
            skLineSegment(sketch, "E162", {"start": v(0, 0) * mm, "end": v(-0.05, 0) * mm});
            skLineSegment(sketch, "E163", {"start": v(-0.05, 0) * mm, "end": v(-0.05, 3.05) * mm});
            skLineSegment(sketch, "E164.bottom", {"start": v(-0.05, 3.05) * mm, "end": v(-44.95, 3.05) * mm});
            skLineSegment(sketch, "E164.top", {"start": v(-0.05, 12.6) * mm, "end": v(-44.95, 12.6) * mm});
            skLineSegment(sketch, "E164.left", {"start": v(-0.05, 3.05) * mm, "end": v(-0.05, 12.6) * mm});
            skLineSegment(sketch, "E164.right", {"start": v(-44.95, 3.05) * mm, "end": v(-44.95, 12.6) * mm});
            skLineSegment(sketch, "E165.top", {"start": v(-0.05, 18.6) * mm, "end": v(-44.95, 18.6) * mm});
            skLineSegment(sketch, "E165.left", {"start": v(-0.05, 3.05) * mm, "end": v(-0.05, 18.6) * mm});
            skLineSegment(sketch, "E165.right", {"start": v(-44.95, 3.05) * mm, "end": v(-44.95, 18.6) * mm});
            skLineSegment(sketch, "E166.top", {"start": v(-0.05, 29.7) * mm, "end": v(-44.95, 29.7) * mm});
            skLineSegment(sketch, "E166.left", {"start": v(-0.05, 3.05) * mm, "end": v(-0.05, 29.7) * mm});
            skLineSegment(sketch, "E166.right", {"start": v(-44.95, 3.05) * mm, "end": v(-44.95, 29.7) * mm});
            skSolve(sketch);
        }
        {
            var Q0;
            {var subQ0=sQuery(id+"F11.wireOp",EDGE,"E164.top");Q0=makeQuery(id+"F11.imprint","IMPRINT",FACE,{"disambiguationData":[TD([[makeQuery(id+"F11.imprint","IMPRINT",EDGE,{"derivedFrom":subQ0}),1.0]])]});}
            extrude(context, id + "F12", {"entities" : qUnion([Q0]), "operationType" : NewBodyOperationType.REMOVE, "depth" : 70 * mm, "hasSecondDirection" : true, "secondDirectionOppositeDirection" : false, "secondDirectionDepth" : 62.05 * mm});
        }
        {
            var Q0;
            {var subQ0=sQuery(id+"F11.wireOp",EDGE,"E164.top");Q0=makeQuery(id+"F11.imprint","IMPRINT",FACE,{"disambiguationData":[TD([[makeQuery(id+"F11.imprint","IMPRINT",EDGE,{"derivedFrom":subQ0}),-1.0]])]});}
            var Q1;
            {var subQ0=sQuery(id+"F11.wireOp",EDGE,"E164.top");Q1=makeQuery(id+"F11.imprint","IMPRINT",FACE,{"disambiguationData":[TD([[makeQuery(id+"F11.imprint","IMPRINT",EDGE,{"derivedFrom":subQ0}),1.0]])]});}
            extrude(context, id + "F13", {"entities" : qUnion([Q0, Q1]), "operationType" : NewBodyOperationType.REMOVE, "depth" : 51 * mm, "hasSecondDirection" : true, "secondDirectionOppositeDirection" : false, "secondDirectionDepth" : 39.05 * mm});
        }
        {
            var Q0;
            Q0 = qSketchRegion(id + "F11", true);
            extrude(context, id + "F14", {"entities" : qUnion([Q0]), "operationType" : NewBodyOperationType.REMOVE, "depth" : 25 * mm, "hasSecondDirection" : true, "secondDirectionOppositeDirection" : false, "secondDirectionDepth" : 13.05 * mm});
        }
    });
